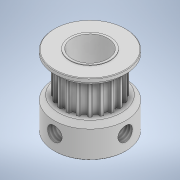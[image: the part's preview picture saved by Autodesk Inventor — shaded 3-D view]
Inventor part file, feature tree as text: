
AUTODESK INVENTOR PART (.ipt)
format: ipt  version: 2020 (Build 240168000, 168)  size: 304,640 bytes
history: native  units: mm
features: sketch x4, plane x3, extrude x2, mirror x2, chamfer x2, projected_geometry x2, revolve x1, hole x1, pattern_circular x1
ambient origin geometry x8: Origin, YZ Plane, XZ Plane, XY Plane, X Axis, Y Axis, Z Axis, Center Point
bodies: Solid1 (feature_tree)
feature tree (18):
  revolve  "Revolution1"  [1 undecoded]
  extrude  "Extrusion1"  Depth=7.0mm
  plane  "Work Plane1"
  mirror  "Mirror1"
  chamfer  "Chamfer2"  Angle=90.0deg  [1 undecoded]
  chamfer  "Chamfer1"  Distance=0.5mm
  plane  "Work Plane2"
  hole  "Hole1"  [1 undecoded]
  plane  "Work Plane3"
  mirror  "Mirror2"
  extrude  "Extrusion2"  Depth=0.1mm TaperAngle=45.0deg
  pattern_circular  "Circular Pattern1"  [2 undecoded]
  sketch  "Sketch1"  dims[d0=8.0mm d1=4.0mm]
  sketch  "Sketch2"  dims[d2=16.0mm d3=7.0mm]
  projected_geometry  "Projected Loop1"
  sketch  "Sketch3"  dims[d4=7.1mm]
  sketch  "Sketch5"  dims[d5=6.11mm d6=90.0deg d7=0.5mm d8=0.1mm d9=0.0mm d10=0.125mm d11=2.0mm d12=45.0deg d13=3.242mm d14=8.0mm d15=5.5mm d16=2.0mm d17=90.0deg d18=11.8mm d19=20.594885mm d22=12.22mm d23=0.15mm d24=0.555mm d25=0.75mm d26=0.1mm d27=0.0mm d28=200.0mm d29=360.0deg d31=1.0mm d32=2.0mm d33=45.0deg]
  projected_geometry  "Project Cut Edges2"
note: 5 required parameter values undecoded (feature->parameter linkage not recoverable at this tier; creation-order binding heuristic only, values carry confidence <= 0.55)